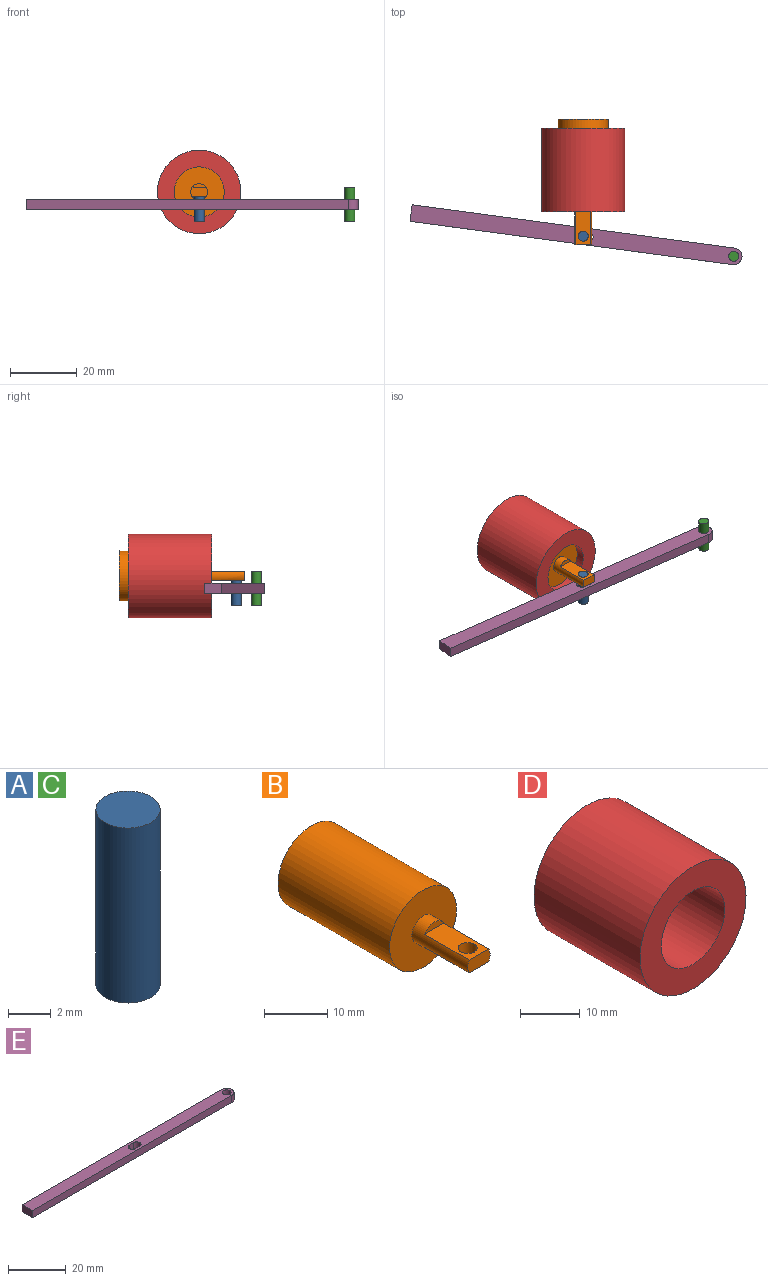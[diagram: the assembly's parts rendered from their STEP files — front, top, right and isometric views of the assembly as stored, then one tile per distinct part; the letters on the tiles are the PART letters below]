
ASSEMBLY  parts=5 mates=4
PART A: 3 faces, bbox 3x3x10 mm
  f0: cylinder r=1.5mm len=10mm, axis (0,0,-1), area 94.2mm2, adj f1,f2
  f1: plane 3x3mm, normal (0,0,1), area 7.1mm2, adj f0
  f2: plane 3x3mm, normal (0,0,-1), area 7.1mm2, adj f0
PART B: 12 faces, bbox 15x37.5x15 mm
  f0: plane 5x2.5mm, normal (0,-1,0), area 12mm2, adj f5,f7,f9
  f1: cylinder r=2.5mm len=12.5mm, axis (0,1,0), area 196.3mm2, adj f4,f6
  f2: cylinder r=7.5mm len=25mm, axis (0,1,0), area 1178.1mm2, adj f3,f4
  f3: plane 15x15mm, normal (0,-1,0), area 157.1mm2, adj f2,f5
  f4: plane 15x15mm, normal (0,1,0), area 157.1mm2, adj f1,f2
  f5: cylinder r=2.5mm len=12.5mm, axis (0,1,0), area 91.6mm2, adj f0,f3,f7,f8,f9,f10
  f6: plane 5x5mm, normal (0,1,0), area 19.6mm2, adj f1
  f7: plane 10x4.33mm, normal (0,0,1), area 36.2mm2, adj f0,f5,f8,f11
  f8: plane 4.33x1.25mm, normal (0,-1,0), area 3.8mm2, adj f5,f7
  f9: plane 10x4.33mm, normal (0,0,-1), area 36.2mm2, adj f0,f5,f10,f11
  f10: plane 4.33x1.25mm, normal (0,-1,0), area 3.8mm2, adj f5,f9
  f11: cylinder r=1.5mm len=3mm, axis (0,0,-1), area 23.6mm2, adj f7,f9
PART C: same geometry as A
PART D: 4 faces, bbox 25x25x25 mm
  f0: cylinder r=7.5mm len=25mm, axis (0,1,0), area 1178.1mm2, adj f2,f3
  f1: cylinder r=12.5mm len=25mm, axis (0,1,0), area 1963.5mm2, adj f2,f3
  f2: plane 25x25mm, normal (0,-1,0), area 314.2mm2, adj f0,f1
  f3: plane 25x25mm, normal (0,1,0), area 314.2mm2, adj f0,f1
PART E: 11 faces, bbox 100x5x3 mm
  f0: plane 97.5x3mm, normal (0,-1,0), area 292.5mm2, adj f1,f6,f9,f10
  f1: cylinder r=2.5mm len=5mm, axis (0,0,-1), area 23.6mm2, adj f0,f2,f9,f10
  f2: plane 97.5x3mm, normal (0,1,0), area 292.5mm2, adj f1,f6,f9,f10
  f3: cylinder r=1.5mm len=3mm, axis (0,0,-1), area 14.1mm2, adj f4,f7,f9,f10
  f4: plane 3x2mm, normal (0,-1,0), area 6mm2, adj f3,f5,f9,f10
  f5: cylinder r=1.5mm len=3mm, axis (0,0,-1), area 14.1mm2, adj f4,f7,f9,f10
  f6: plane 5x3mm, normal (-1,0,0), area 15mm2, adj f0,f2,f9,f10
  f7: plane 3x2mm, normal (0,1,0), area 6mm2, adj f3,f5,f9,f10
  f8: cylinder r=1.5mm len=3mm, axis (0,0,-1), area 28.3mm2, adj f9,f10
  f9: plane 100x5mm, normal (0,0,1), area 477.2mm2, adj f0,f1,f2,f3,f4,f5,f6,f7
  f10: plane 100x5mm, normal (0,0,-1), area 477.2mm2, adj f0,f1,f2,f3,f4,f5,f6,f7
PLACE A rot(axis=(0,0,1),24.6deg) t=(-50.61,-14.74,14.3)mm
PLACE B t=(-7.42,-2.46,6.11)mm
PLACE C rot(axis=(0,0,-1),0deg) t=(-9.85,-1.01,14.3)mm fixed
PLACE D t=(-7.42,-5.1,6.11)mm fixed
PLACE E rot(axis=(0,0,-1),7.6deg) t=(-9.43,5.31,12.8)mm
MATE slider D.f0 <-> B.f1  axis (0,1,0) through (-7.42,24.9,18.05)mm
MATE revolute A.f0 <-> B.f11  axis (0,0,1) through (-7.42,5.04,19.3)mm
MATE pin_slot A.f0 <-> E.f3  axis (0,0,-1) through (-7.42,5.04,14.3)mm
MATE revolute E.f1 <-> C.f0  axis (0,0,-1) through (37.65,-1.01,14.3)mm
